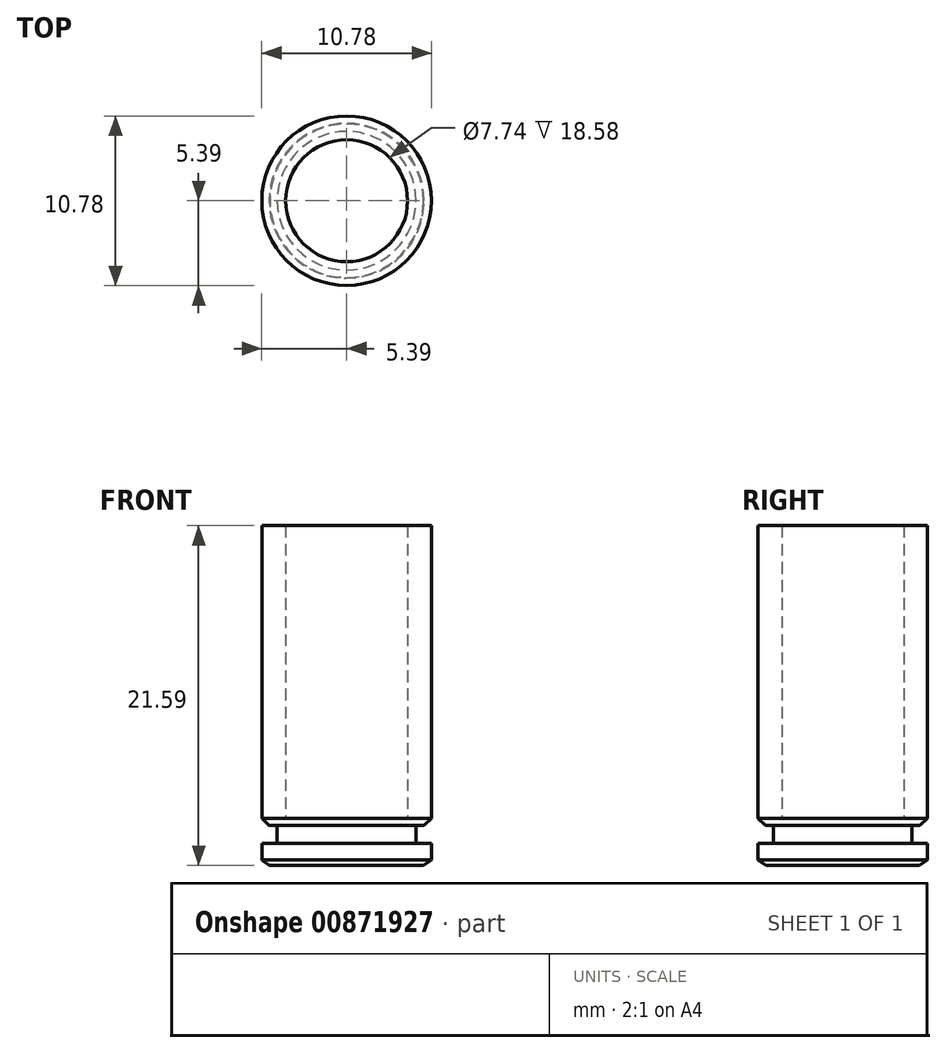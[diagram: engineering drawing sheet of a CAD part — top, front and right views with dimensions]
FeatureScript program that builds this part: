
annotation { "Feature Type Name" : "Feature", "Feature Type Description" : "" }
export const myFeature = defineFeature(function(context is Context, id is Id, definition is map)
    precondition{}
    {
        {
            var Q0;
            Q0=qCreatedBy(makeId("Top.planeOp"),FACE);
            var sketch = newSketch(context, id + "F0", { "sketchPlane" : qUnion([Q0])});
            skCircle(sketch, "E0", {"center": v(0, 0) * mm, "radius": 5.38 * mm});
            skCircle(sketch, "E1", {"center": v(0, 0) * mm, "radius": 3.87 * mm});
            skSolve(sketch);
        }
        {
            var Q0;
            Q0 = qSketchRegion(id + "F0", true);
            extrude(context, id + "F1", {"entities" : qUnion([Q0]), "depth" : 18.58 * mm, "offsetDistance" : 25 * mm});
        }
        {
            var Q0;
            Q0=makeQuery(id+"F1.opExtrude","CAP_FACE",FACE,{"disambiguationData":[OSD([sQuery(id+"F0.wireOp",EDGE,"E0"),sQuery(id+"F0.wireOp",EDGE,"E1")])],"isStart":true});
            var sketch = newSketch(context, id + "F2", { "sketchPlane" : qUnion([Q0])});
            skCircle(sketch, "E2", {"center": v(0, 0) * mm, "radius": 5.38 * mm});
            skSolve(sketch);
        }
        {
            var Q0;
            Q0 = qSketchRegion(id + "F2", true);
            extrude(context, id + "F3", {"entities" : qUnion([Q0]), "operationType" : NewBodyOperationType.ADD, "depth" : .47 * mm, "offsetDistance" : 25 * mm});
        }
        {
            var Q0;
            Q0=makeQuery(id+"F3.opExtrude","CAP_EDGE",EDGE,{"disambiguationData":[OSD([sQuery(id+"F2.wireOp",EDGE,"E2")])],"isStart":false});
            chamfer(context, id + "F4", {"entities" : qUnion([Q0]), "chamferType" : ChamferType.OFFSET_ANGLE, "width" : .47 * mm, "oppositeDirection" : false, "angle" : 45 * degree, "tangentPropagation" : true});
        }
        {
            var Q0;
            Q0=makeQuery(id+"F3.opExtrude","CAP_FACE",FACE,{"disambiguationData":[OSD([sQuery(id+"F2.wireOp",EDGE,"E2")])],"isStart":false});
            var sketch = newSketch(context, id + "F5", { "sketchPlane" : qUnion([Q0])});
            skCircle(sketch, "E3", {"center": v(0, 0) * mm, "radius": 4.4 * mm});
            skSolve(sketch);
        }
        {
            var Q0;
            Q0 = qSketchRegion(id + "F5", true);
            extrude(context, id + "F6", {"entities" : qUnion([Q0]), "operationType" : NewBodyOperationType.ADD, "depth" : 1.14 * mm, "offsetDistance" : 25 * mm});
        }
        {
            var Q0;
            Q0=makeQuery(id+"F6.opExtrude","CAP_FACE",FACE,{"disambiguationData":[OSD([sQuery(id+"F5.wireOp",EDGE,"E3")])],"isStart":false});
            var sketch = newSketch(context, id + "F7", { "sketchPlane" : qUnion([Q0])});
            skCircle(sketch, "E4", {"center": v(0, 0) * mm, "radius": 5.38 * mm});
            skSolve(sketch);
        }
        {
            var Q0;
            Q0 = qSketchRegion(id + "F7", true);
            extrude(context, id + "F8", {"entities" : qUnion([Q0]), "operationType" : NewBodyOperationType.ADD, "depth" : 1.4 * mm, "offsetDistance" : 25 * mm});
        }
        {
            var Q0;
            Q0=makeQuery(id+"F8.opExtrude","CAP_EDGE",EDGE,{"disambiguationData":[OSD([sQuery(id+"F7.wireOp",EDGE,"E4")])],"isStart":false});
            chamfer(context, id + "F9", {"entities" : qUnion([Q0]), "chamferType" : ChamferType.OFFSET_ANGLE, "width" : .51 * mm, "oppositeDirection" : false, "angle" : 35 * degree, "tangentPropagation" : true});
        }
    });
